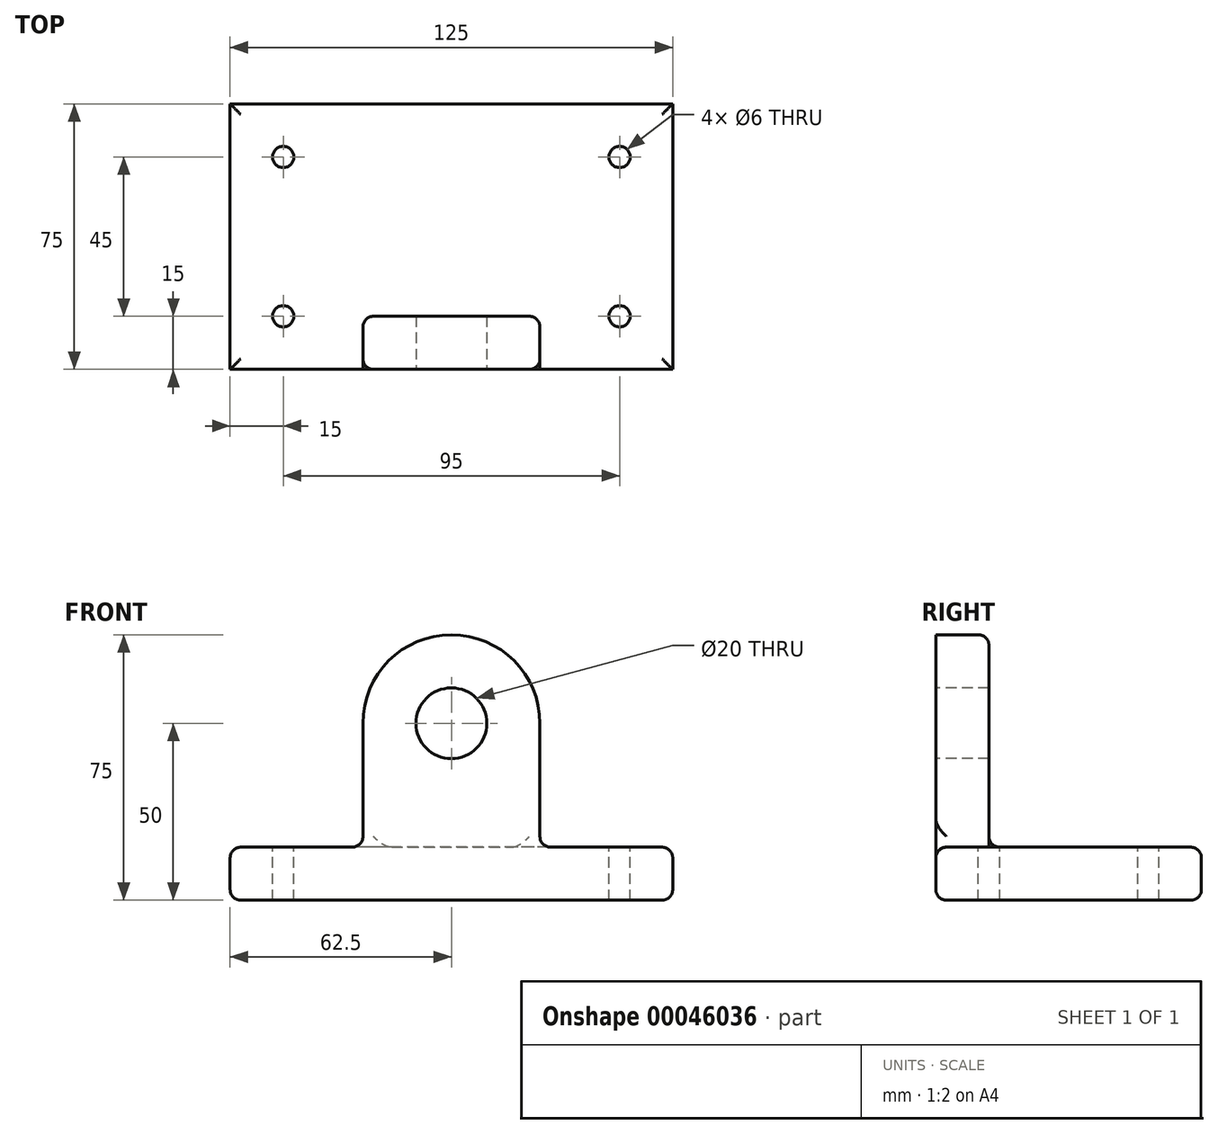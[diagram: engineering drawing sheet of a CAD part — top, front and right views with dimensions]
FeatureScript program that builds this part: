
annotation { "Feature Type Name" : "Feature", "Feature Type Description" : "" }
export const myFeature = defineFeature(function(context is Context, id is Id, definition is map)
    precondition{}
    {
        {
            var Q0;
            Q0=qCreatedBy(makeId("Top.planeOp"),FACE);
            var sketch = newSketch(context, id + "F0", { "sketchPlane" : qUnion([Q0])});
            skLineSegment(sketch, "E0.rect.bottom", {"start": v(62.5, -37.5) * mm, "end": v(-62.5, -37.5) * mm});
            skLineSegment(sketch, "E0.rect.top", {"start": v(62.5, 37.5) * mm, "end": v(-62.5, 37.5) * mm});
            skLineSegment(sketch, "E0.rect.left", {"start": v(62.5, -37.5) * mm, "end": v(62.5, 37.5) * mm});
            skLineSegment(sketch, "E0.rect.right", {"start": v(-62.5, -37.5) * mm, "end": v(-62.5, 37.5) * mm});
            skPoint(sketch, "E0.rect.middle", {"position": v(0, 0) * mm});
            skSolve(sketch);
        }
        {
            var Q0;
            Q0=makeQuery(id+"F0.imprint","IMPRINT",FACE,{"disambiguationData":[TD([[makeQuery(id+"F0.imprint","IMPRINT",EDGE,{"derivedFrom":sQuery(id+"F0.wireOp",EDGE,"E0.rect.bottom")}),-1.0]])]});
            extrude(context, id + "F1", {"entities" : qUnion([Q0]), "depth" : 15 * mm});
        }
        {
            var Q0;
            Q0=makeQuery(id+"F1.opExtrude","SWEPT_FACE",FACE,{"disambiguationData":[OSD([sQuery(id+"F0.wireOp",EDGE,"E0.rect.bottom")])]});
            var sketch = newSketch(context, id + "F2", { "sketchPlane" : qUnion([Q0])});
            skLineSegment(sketch, "E1", {"start": v(0, 0) * mm, "end": v(0, 50) * mm, "construction": true});
            skPoint(sketch, "E1.endSnap0", {"position": v(0, 15) * mm});
            skCircle(sketch, "E2", {"center": v(0, 50) * mm, "radius": 25 * mm});
            skLineSegment(sketch, "E3.bottom", {"start": v(-25, 50) * mm, "end": v(25, 50) * mm});
            skLineSegment(sketch, "E3.top", {"start": v(-25, 0) * mm, "end": v(25, 0) * mm});
            skLineSegment(sketch, "E3.left", {"start": v(-25, 50) * mm, "end": v(-25, 0) * mm});
            skLineSegment(sketch, "E3.right", {"start": v(25, 50) * mm, "end": v(25, 0) * mm});
            skCircle(sketch, "E4", {"center": v(0, 50) * mm, "radius": 10 * mm});
            skSolve(sketch);
        }
        {
            var Q0;
            {var subQ7=sQuery(id+"F2.wireOp",EDGE,"E3.top");Q0=makeQuery(id+"F2.imprint","IMPRINT",FACE,{"disambiguationData":[TD([[makeQuery(id+"F2.imprint","IMPRINT",EDGE,{"derivedFrom":subQ7}),-1.0]])]});}
            var Q1;
            {var subQ0=sQuery(id+"F2.wireOp",EDGE,"E3.left");var subQ1=makeQuery(id+"F1.opExtrude","CAP_EDGE",EDGE,{"disambiguationData":[OSD([sQuery(id+"F0.wireOp",EDGE,"E0.rect.bottom")])],"isStart":false});var subQ2=makeQuery(id+"F2.imprint","INTERSECT",VERTEX,{"derivedFrom":[subQ1,subQ0]});Q1=makeQuery(id+"F2.imprint","IMPRINT",FACE,{"disambiguationData":[TD([[makeQuery(id+"F2.imprint","IMPRINT",EDGE,{"disambiguationData":[TD([[subQ2,1.0]])],"derivedFrom":subQ1}),-1.0]])]});}
            var Q2;
            {var subQ0=sQuery(id+"F2.wireOp",EDGE,"E3.bottom");var subQ1=sQuery(id+"F2.wireOp",EDGE,"E4");var subQ5=makeQuery(id+"F2.imprint","INTERSECT",VERTEX,{"disambiguationData":[OD(0.0)],"derivedFrom":[subQ0,subQ1]});Q2=makeQuery(id+"F2.imprint","IMPRINT",FACE,{"disambiguationData":[TD([[makeQuery(id+"F2.imprint","IMPRINT",EDGE,{"disambiguationData":[TD([[subQ5,-1.0]])],"derivedFrom":subQ1}),-1.0]])]});}
            var Q3;
            {var subQ0=sQuery(id+"F2.wireOp",EDGE,"E3.bottom");var subQ1=sQuery(id+"F2.wireOp",EDGE,"E4");var subQ5=makeQuery(id+"F2.imprint","INTERSECT",VERTEX,{"disambiguationData":[OD(0.0)],"derivedFrom":[subQ0,subQ1]});Q3=makeQuery(id+"F2.imprint","IMPRINT",FACE,{"disambiguationData":[TD([[makeQuery(id+"F2.imprint","IMPRINT",EDGE,{"disambiguationData":[TD([[subQ5,1.0]])],"derivedFrom":subQ1}),-1.0]])]});}
            extrude(context, id + "F3", {"entities" : qUnion([Q0, Q1, Q2, Q3]), "operationType" : NewBodyOperationType.ADD, "oppositeDirection" : true, "depth" : 15 * mm});
        }
        {
            var Q0;
            Q0=makeQuery(id+"F1.opExtrude","CAP_FACE",FACE,{"disambiguationData":[OSD([sQuery(id+"F0.wireOp",EDGE,"E0.rect.bottom"),sQuery(id+"F0.wireOp",EDGE,"E0.rect.top"),sQuery(id+"F0.wireOp",EDGE,"E0.rect.left"),sQuery(id+"F0.wireOp",EDGE,"E0.rect.right")])],"isStart":false});
            var sketch = newSketch(context, id + "F4", { "sketchPlane" : qUnion([Q0])});
            skLineSegment(sketch, "E5.rect.bottom", {"start": v(47.5, -22.5) * mm, "end": v(-47.5, -22.5) * mm, "construction": true});
            skLineSegment(sketch, "E5.rect.top", {"start": v(47.5, 22.5) * mm, "end": v(-47.5, 22.5) * mm, "construction": true});
            skLineSegment(sketch, "E5.rect.left", {"start": v(47.5, -22.5) * mm, "end": v(47.5, 22.5) * mm, "construction": true});
            skLineSegment(sketch, "E5.rect.right", {"start": v(-47.5, -22.5) * mm, "end": v(-47.5, 22.5) * mm, "construction": true});
            skPoint(sketch, "E5.rect.middle", {"position": v(0, 0) * mm});
            skCircle(sketch, "E6", {"center": v(-47.5, 22.5) * mm, "radius": 3 * mm});
            skCircle(sketch, "E7", {"center": v(-47.5, -22.5) * mm, "radius": 3 * mm});
            skCircle(sketch, "E8", {"center": v(47.5, 22.5) * mm, "radius": 3 * mm});
            skCircle(sketch, "E9", {"center": v(47.5, -22.5) * mm, "radius": 3 * mm});
            skSolve(sketch);
        }
        {
            var Q0;
            Q0=makeQuery(id+"F4.imprint","IMPRINT",FACE,{"disambiguationData":[TD([[makeQuery(id+"F4.imprint","IMPRINT",EDGE,{"derivedFrom":sQuery(id+"F4.wireOp",EDGE,"E6")}),1.0]])]});
            var Q1;
            Q1=makeQuery(id+"F4.imprint","IMPRINT",FACE,{"disambiguationData":[TD([[makeQuery(id+"F4.imprint","IMPRINT",EDGE,{"derivedFrom":sQuery(id+"F4.wireOp",EDGE,"E7")}),1.0]])]});
            var Q2;
            Q2=makeQuery(id+"F4.imprint","IMPRINT",FACE,{"disambiguationData":[TD([[makeQuery(id+"F4.imprint","IMPRINT",EDGE,{"derivedFrom":sQuery(id+"F4.wireOp",EDGE,"E8")}),1.0]])]});
            var Q3;
            Q3=makeQuery(id+"F4.imprint","IMPRINT",FACE,{"disambiguationData":[TD([[makeQuery(id+"F4.imprint","IMPRINT",EDGE,{"derivedFrom":sQuery(id+"F4.wireOp",EDGE,"E9")}),1.0]])]});
            extrude(context, id + "F5", {"entities" : qUnion([Q0, Q1, Q2, Q3]), "operationType" : NewBodyOperationType.REMOVE, "endBound" : BoundingType.THROUGH_ALL, "oppositeDirection" : true, "depth" : 25 * mm});
        }
        {
            var Q0;
            {var subQ0=sQuery(id+"F0.wireOp",EDGE,"E0.rect.bottom");var subQ2=sQuery(id+"F0.wireOp",EDGE,"E0.rect.right");Q0=makeQuery(id+"F3.boolean.opBoolean","SPLIT",EDGE,{"disambiguationData":[TD([makeQuery(id+"F1.opExtrude","SWEPT_FACE",FACE,{"disambiguationData":[OSD([subQ2])]})])],"derivedFrom":makeQuery(id+"F1.opExtrude","CAP_EDGE",EDGE,{"disambiguationData":[OSD([subQ0])],"isStart":false})});}
            var Q1;
            Q1=makeQuery(id+"F1.opExtrude","CAP_EDGE",EDGE,{"disambiguationData":[OSD([sQuery(id+"F0.wireOp",EDGE,"E0.rect.right")])],"isStart":false});
            var Q2;
            Q2=makeQuery(id+"F1.opExtrude","CAP_EDGE",EDGE,{"disambiguationData":[OSD([sQuery(id+"F0.wireOp",EDGE,"E0.rect.top")])],"isStart":false});
            var Q3;
            Q3=makeQuery(id+"F1.opExtrude","CAP_EDGE",EDGE,{"disambiguationData":[OSD([sQuery(id+"F0.wireOp",EDGE,"E0.rect.left")])],"isStart":false});
            var Q4;
            {var subQ0=sQuery(id+"F0.wireOp",EDGE,"E0.rect.bottom");var subQ2=sQuery(id+"F0.wireOp",EDGE,"E0.rect.left");Q4=makeQuery(id+"F3.boolean.opBoolean","SPLIT",EDGE,{"disambiguationData":[TD([makeQuery(id+"F1.opExtrude","SWEPT_FACE",FACE,{"disambiguationData":[OSD([subQ2])]})])],"derivedFrom":makeQuery(id+"F1.opExtrude","CAP_EDGE",EDGE,{"disambiguationData":[OSD([subQ0])],"isStart":false})});}
            var Q5;
            Q5=makeQuery(id+"F3.boolean.opBoolean","INTERSECT",EDGE,{"derivedFrom":[makeQuery(id+"F1.opExtrude","CAP_FACE",FACE,{"disambiguationData":[OSD([sQuery(id+"F0.wireOp",EDGE,"E0.rect.bottom"),sQuery(id+"F0.wireOp",EDGE,"E0.rect.top"),sQuery(id+"F0.wireOp",EDGE,"E0.rect.left"),sQuery(id+"F0.wireOp",EDGE,"E0.rect.right")])],"isStart":false}),makeQuery(id+"F3.opExtrude","SWEPT_FACE",FACE,{"disambiguationData":[OSD([sQuery(id+"F2.wireOp",EDGE,"E3.right")])]})]});
            var Q6;
            Q6=makeQuery(id+"F3.boolean.opBoolean","INTERSECT",EDGE,{"derivedFrom":[makeQuery(id+"F1.opExtrude","CAP_FACE",FACE,{"disambiguationData":[OSD([sQuery(id+"F0.wireOp",EDGE,"E0.rect.bottom"),sQuery(id+"F0.wireOp",EDGE,"E0.rect.top"),sQuery(id+"F0.wireOp",EDGE,"E0.rect.left"),sQuery(id+"F0.wireOp",EDGE,"E0.rect.right")])],"isStart":false}),makeQuery(id+"F3.opExtrude","SWEPT_FACE",FACE,{"disambiguationData":[OSD([sQuery(id+"F2.wireOp",EDGE,"E3.left")])]})]});
            var Q7;
            Q7=makeQuery(id+"F3.opExtrude","CAP_EDGE",EDGE,{"disambiguationData":[OSD([sQuery(id+"F2.wireOp",EDGE,"E3.left")])],"isStart":false});
            var Q8;
            Q8=makeQuery(id+"F1.opExtrude","CAP_EDGE",EDGE,{"disambiguationData":[OSD([sQuery(id+"F0.wireOp",EDGE,"E0.rect.bottom")])],"isStart":true});
            var Q9;
            Q9=makeQuery(id+"F1.opExtrude","CAP_EDGE",EDGE,{"disambiguationData":[OSD([sQuery(id+"F0.wireOp",EDGE,"E0.rect.left")])],"isStart":true});
            var Q10;
            Q10=makeQuery(id+"F1.opExtrude","CAP_EDGE",EDGE,{"disambiguationData":[OSD([sQuery(id+"F0.wireOp",EDGE,"E0.rect.top")])],"isStart":true});
            var Q11;
            Q11=makeQuery(id+"F1.opExtrude","CAP_EDGE",EDGE,{"disambiguationData":[OSD([sQuery(id+"F0.wireOp",EDGE,"E0.rect.right")])],"isStart":true});
            fillet(context, id + "F6", {"entities" : qUnion([Q0, Q1, Q2, Q3, Q4, Q5, Q6, Q7, Q8, Q9, Q10, Q11]), "radius" : 3 * mm, "tangentPropagation" : true, "allowEdgeOverflow" : false});
        }
    });
